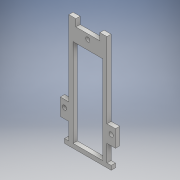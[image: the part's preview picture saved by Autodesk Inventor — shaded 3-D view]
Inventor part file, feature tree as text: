
AUTODESK INVENTOR PART (.ipt)
format: ipt  version: 2017 (Build 210142000, 142)  size: 153,600 bytes
history: native  units: mm
features: other x3, extrude x1, sketch x1
ambient origin geometry x8: Origin, YZ Plane, XZ Plane, XY Plane, X Axis, Y Axis, Z Axis, Center Point
bodies: Solid1 (feature_tree)
feature tree (5):
  other  "k2_t_l3.ipt"
  extrude  "Extrusion1"  Depth=12.0mm TaperAngle=0.0deg
  other  "Solid1::k2_t_l3.ipt"
  other  "TaggingFeature1"
  sketch  "Sketch1"  dims[d0=10.0mm d6=3.0mm d15=0.0mm d16=3.0mm d18=2.517299mm d19=0.0mm d21=21.0mm d2=3.0mm d3=0.0mm d8=3.0mm d9=3.0mm d11=33.0mm d12=12.0mm d13=60.415173mm d14=12.0mm d10=2.517299mm d17=0.0mm]
